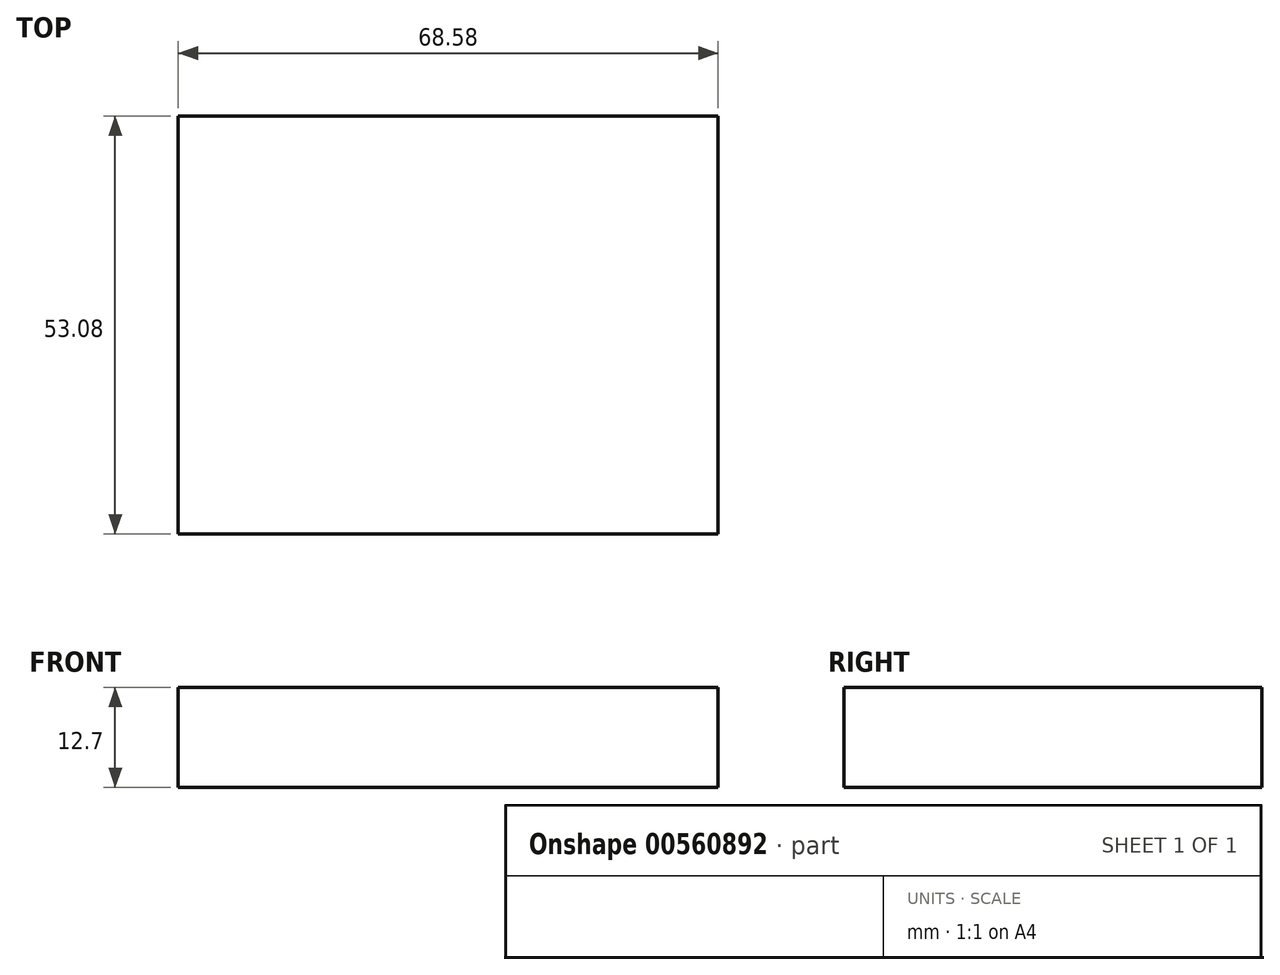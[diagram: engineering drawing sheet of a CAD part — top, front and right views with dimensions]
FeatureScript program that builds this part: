
annotation { "Feature Type Name" : "Feature", "Feature Type Description" : "" }
export const myFeature = defineFeature(function(context is Context, id is Id, definition is map)
    precondition{}
    {
        {
            var Q0;
            Q0=qCreatedBy(makeId("Top.planeOp"),FACE);
            var sketch = newSketch(context, id + "F0", { "sketchPlane" : qUnion([Q0])});
            skLineSegment(sketch, "E0.bottom", {"start": v(-34.3, 26.54) * mm, "end": v(34.3, 26.54) * mm});
            skLineSegment(sketch, "E0.top", {"start": v(-34.3, -26.54) * mm, "end": v(34.3, -26.54) * mm});
            skLineSegment(sketch, "E0.left", {"start": v(-34.3, 26.54) * mm, "end": v(-34.3, -26.54) * mm});
            skLineSegment(sketch, "E0.right", {"start": v(34.3, 26.54) * mm, "end": v(34.3, -26.54) * mm});
            skPoint(sketch, "E0.middle", {"position": v(0, 0) * mm});
            skSolve(sketch);
        }
        {
            var Q0;
            Q0 = qSketchRegion(id + "F0", true);
            extrude(context, id + "F1", {"entities" : qUnion([Q0]), "depth" : 12.7 * mm, "offsetDistance" : 25.4 * mm});
        }
    });
